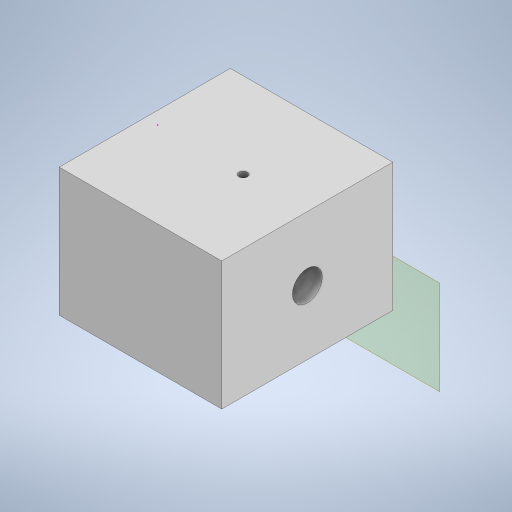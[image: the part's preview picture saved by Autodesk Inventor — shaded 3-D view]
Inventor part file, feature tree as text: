
AUTODESK INVENTOR PART (.ipt)
format: ipt  version: 2023 (Build 270158000, 158)  size: 288,768 bytes
history: native  units: mm
features: sketch x9, extrude x7, plane x6
ambient origin geometry x8: Origin, YZ Plane, XZ Plane, XY Plane, X Axis, Y Axis, Z Axis, Center Point
bodies: Body1 (feature_tree)
feature tree (22):
  plane  "Work Plane13"
  extrude  "Extrusion34"  Depth=40.0mm
  sketch  "Sketch46"  dims[d144=30.0mm d145=0.0mm d146=36.0mm]
  plane  "Work Plane11"
  extrude  "Extrusion35"  Depth=36.0mm
  sketch  "Sketch48"  dims[d150=0.0mm d151=0.0mm d156=20.0mm]
  extrude  "Extrusion36"  Depth=2.0mm
  plane  "Work Plane7"
  extrude  "Extrusion38"  Depth=20.0mm
  plane  "Work Plane4"
  extrude  "Extrusion39"  Depth=15.0mm TaperAngle=0.0deg
  plane  "Work Plane1"
  plane  "Work Plane6"
  extrude  "Extrusion42"  Depth=20.0mm
  extrude  "Extrusion44"  Depth=7.0mm
  sketch  "Sketch45"  dims[d142=38.0mm d143=40.0mm]
  sketch  "Sketch47"  dims[d147=30.0mm d148=-2.617994mm d149=2.0mm]
  sketch  "Sketch49"  dims[d157=15.0mm d158=15.0mm d159=0.0mm]
  sketch  "Sketch58"  dims[d160=4.0mm d161=20.0mm]
  sketch  "Sketch59"  dims[d162=35.0mm d163=0.0mm d172=7.0mm]
  sketch  "Sketch62"  dims[d173=0.0mm d174=0.0mm]
  sketch  "Sketch65"  dims[d177=5.0mm d178=0.0mm d49=0.5mm d50=0.872665mm d51=0.5mm d52=0.872665mm d130=0.5mm d131=0.872665mm d132=0.5mm d133=0.872665mm]
